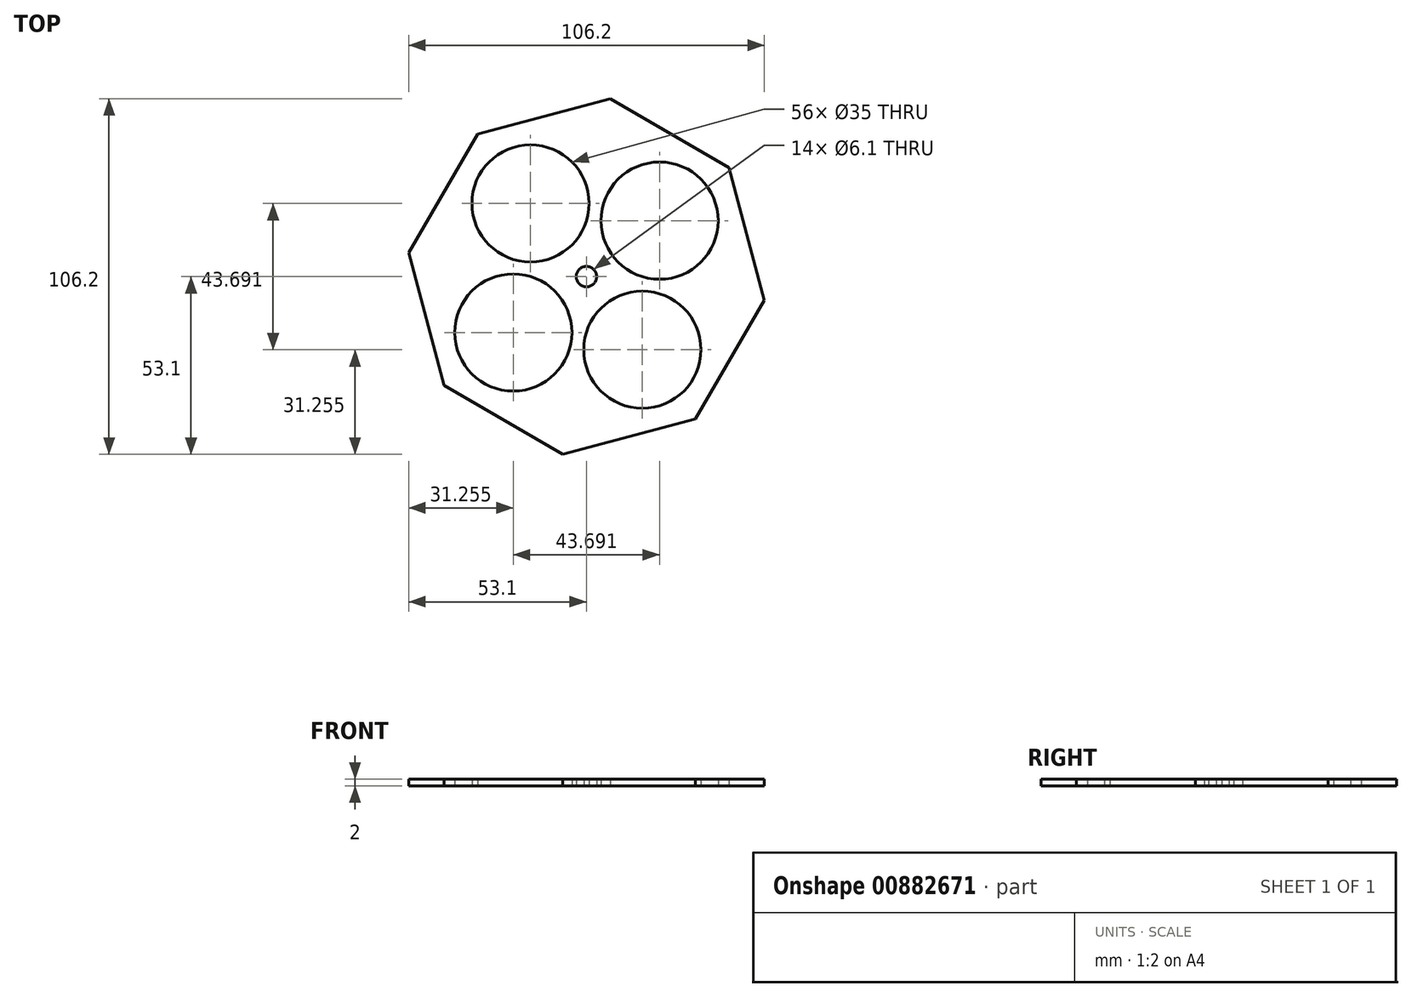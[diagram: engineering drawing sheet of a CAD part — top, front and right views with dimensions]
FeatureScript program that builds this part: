
annotation { "Feature Type Name" : "Feature", "Feature Type Description" : "" }
export const myFeature = defineFeature(function(context is Context, id is Id, definition is map)
    precondition{}
    {
        {
            var Q0;
            Q0=qCreatedBy(makeId("Top.planeOp"),FACE);
            cPlane(context, id + "F0", {"entities" : qUnion([Q0]), "cplaneType" : CPlaneType.OFFSET, "offset" : 200 * mm, "width" : 150 * mm, "height" : 150 * mm});
        }
        {
            var Q0;
            Q0=qCreatedBy(id+"F0.planeOp",FACE);
            var sketch = newSketch(context, id + "F1", { "sketchPlane" : qUnion([Q0])});
            skCircle(sketch, "E0.cCircle", {"center": v(0, 0) * mm, "radius": 49.5 * mm, "construction": true});
            skLineSegment(sketch, "E0.0", {"start": v(-53.1, 7.08) * mm, "end": v(-32.54, 42.55) * mm});
            skLineSegment(sketch, "E0.1", {"start": v(-32.54, 42.55) * mm, "end": v(7.08, 53.1) * mm});
            skLineSegment(sketch, "E0.2", {"start": v(7.08, 53.1) * mm, "end": v(42.55, 32.54) * mm});
            skLineSegment(sketch, "E0.3", {"start": v(42.55, 32.54) * mm, "end": v(53.1, -7.08) * mm});
            skLineSegment(sketch, "E0.4", {"start": v(53.1, -7.08) * mm, "end": v(32.54, -42.55) * mm});
            skLineSegment(sketch, "E0.5", {"start": v(32.54, -42.55) * mm, "end": v(-7.08, -53.1) * mm});
            skLineSegment(sketch, "E0.6", {"start": v(-7.08, -53.1) * mm, "end": v(-42.55, -32.54) * mm});
            skLineSegment(sketch, "E0.7", {"start": v(-42.55, -32.54) * mm, "end": v(-53.1, 7.08) * mm});
            skPoint(sketch, "E0.0.midPoint", {"position": v(-42.82, 24.82) * mm});
            skCircle(sketch, "E1", {"center": v(0, 0) * mm, "radius": 47.1 * mm});
            skLineSegment(sketch, "E2", {"start": v(-32.54, 42.55) * mm, "end": v(32.54, -42.55) * mm, "construction": true});
            skLineSegment(sketch, "E3", {"start": v(42.55, 32.54) * mm, "end": v(-42.55, -32.54) * mm, "construction": true});
            skCircle(sketch, "E4", {"center": v(0, 0) * mm, "radius": 3.05 * mm});
            skCircle(sketch, "E5", {"center": v(0, 0) * mm, "radius": 27.5 * mm, "construction": true});
            skCircle(sketch, "E6", {"center": v(-21.85, -16.7) * mm, "radius": 17.5 * mm});
            skCircle(sketch, "E7.1.0", {"center": v(16.7, -21.85) * mm, "radius": 17.5 * mm});
            skCircle(sketch, "E7.2.0", {"center": v(21.85, 16.7) * mm, "radius": 17.5 * mm});
            skCircle(sketch, "E7.3.0", {"center": v(-16.7, 21.85) * mm, "radius": 17.5 * mm});
            skSolve(sketch);
        }
        {
            var Q0;
            Q0=makeQuery(id+"F1.imprint","IMPRINT",FACE,{"disambiguationData":[TD([[makeQuery(id+"F1.imprint","IMPRINT",EDGE,{"derivedFrom":sQuery(id+"F1.wireOp",EDGE,"E1")}),1.0]])]});
            var Q1;
            Q1=makeQuery(id+"F1.imprint","IMPRINT",FACE,{"disambiguationData":[TD([[makeQuery(id+"F1.imprint","IMPRINT",EDGE,{"derivedFrom":sQuery(id+"F1.wireOp",EDGE,"E0.0")}),-1.0]])]});
            extrude(context, id + "F2", {"entities" : qUnion([Q0, Q1]), "depth" : 2 * mm, "offsetDistance" : 25 * mm});
        }
    });
